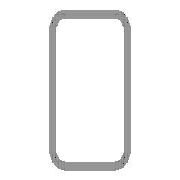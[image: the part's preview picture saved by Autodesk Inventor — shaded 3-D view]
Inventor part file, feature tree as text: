
AUTODESK INVENTOR PART (.ipt)
format: ipt  version: 2025.3 (Build 293356030, 356C)  size: 148,992 bytes
history: native  units: mm (DEFAULTED — no unit token found)
features: other x4, plane x3, split x2, sketch x1
ambient origin geometry x8: Origin, YZ Plane, XZ Plane, XY Plane, X Axis, Y Axis, Z Axis, Center Point
bodies: Solid1 (feature_tree), Body (feature_tree)
feature tree (10):
  parser-record x1  (decoder bookkeeping rows leaked as tree rows — omitted from the tree; the rows remain in map.json)
  other  "Driven Length"
  other  "Start Plane"
  other  "End Plane"
  plane  "Work Plane4"
  split  "Split1"
  plane  "Work Plane5"
  split  "Split2"
  sketch  "Sketch3"  dims[d3=2924.995667mm d4=0.0mm d7=4.0mm d9=20.0mm d11=40.0mm d12=2.0mm d13=73.137085mm d14=2998.132752mm d15=10.0mm d16=20.0mm d17=90.0deg d18=2924.995667mm]
  plane  "Work Plane3"
